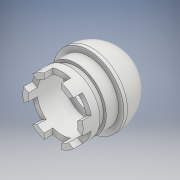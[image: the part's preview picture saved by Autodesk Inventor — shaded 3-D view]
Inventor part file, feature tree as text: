
AUTODESK INVENTOR PART (.ipt)
format: ipt  version: 2018 (Build 220112000, 112)  size: 210,432 bytes
history: native  units: mm
features: sketch x4, revolve x2, extrude x2, pattern_circular x1
ambient origin geometry x8: Origin, YZ Plane, XZ Plane, XY Plane, X Axis, Y Axis, Z Axis, Center Point
bodies: Solid1 (feature_tree)
feature tree (9):
  revolve  "Revolution1"  [1 undecoded]
  extrude  "Extrusion1"  TaperAngle=90.0deg  [1 undecoded]
  pattern_circular  "Circular Pattern1"  [2 undecoded]
  extrude  "Extrusion2"  Depth=10.0mm TaperAngle=0.0deg
  revolve  "Revolution2"  Angle=360.0deg
  sketch  "Sketch1"  dims[d0=3.0mm d1=2.0mm]
  sketch  "Sketch2"  dims[d3=20.0mm d6=90.0deg]
  sketch  "Sketch3"  dims[d7=10.0mm]
  sketch  "Sketch4"  dims[d8=15.0mm d9=20.0mm d10=10.0mm d11=0.0mm d12=60.0mm d13=360.0deg d15=20.0mm d16=15.5mm d17=0.0mm d18=1.5mm d19=3.5mm d20=90.0deg d21=7.0mm d22=3.0mm d23=20.0mm]
note: 4 required parameter values undecoded (feature->parameter linkage not recoverable at this tier; creation-order binding heuristic only, values carry confidence <= 0.55)